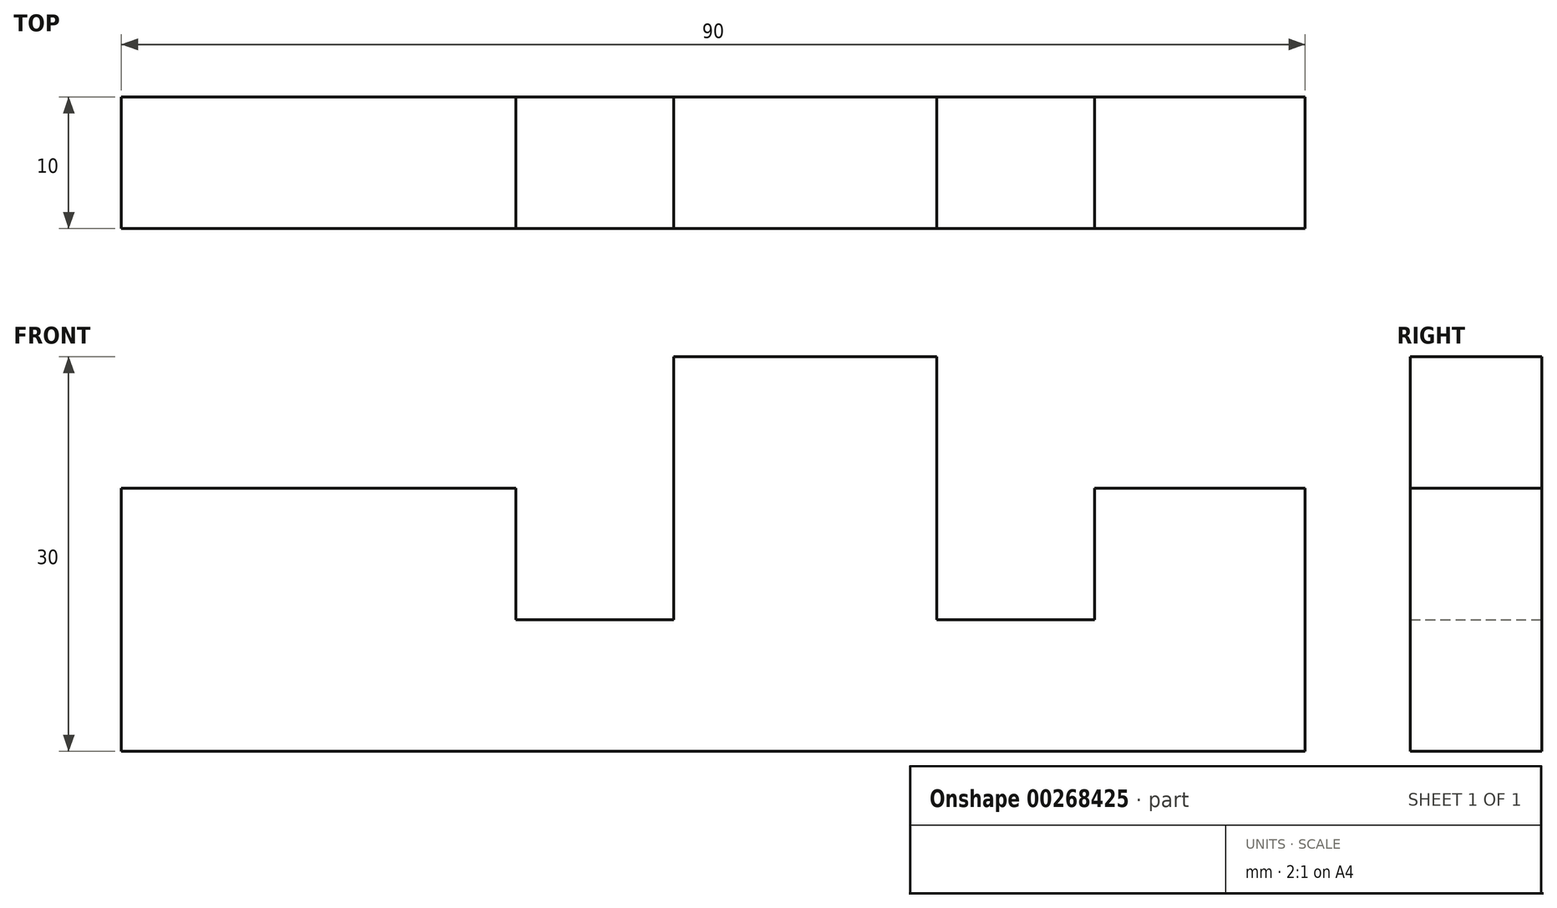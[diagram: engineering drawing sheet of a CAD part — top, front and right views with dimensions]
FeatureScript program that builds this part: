
annotation { "Feature Type Name" : "Feature", "Feature Type Description" : "" }
export const myFeature = defineFeature(function(context is Context, id is Id, definition is map)
    precondition{}
    {
        {
            var Q0;
            Q0=qCreatedBy(makeId("Front.planeOp"),FACE);
            var sketch = newSketch(context, id + "F0", { "sketchPlane" : qUnion([Q0])});
            skLineSegment(sketch, "E0", {"start": v(0, 0) * mm, "end": v(90, 0) * mm});
            skLineSegment(sketch, "E1", {"start": v(0, 0) * mm, "end": v(0, 20) * mm});
            skLineSegment(sketch, "E2", {"start": v(0, 20) * mm, "end": v(30, 20) * mm});
            skLineSegment(sketch, "E3", {"start": v(30, 20) * mm, "end": v(30, 10) * mm});
            skLineSegment(sketch, "E4", {"start": v(30, 10) * mm, "end": v(42, 10) * mm});
            skLineSegment(sketch, "E5", {"start": v(42, 10) * mm, "end": v(42, 30) * mm});
            skLineSegment(sketch, "E6", {"start": v(42, 30) * mm, "end": v(62, 30) * mm});
            skLineSegment(sketch, "E7", {"start": v(62, 30) * mm, "end": v(62, 10) * mm});
            skLineSegment(sketch, "E8", {"start": v(62, 10) * mm, "end": v(74, 10) * mm});
            skLineSegment(sketch, "E9", {"start": v(74, 10) * mm, "end": v(74, 20) * mm});
            skLineSegment(sketch, "E10", {"start": v(74, 20) * mm, "end": v(90, 20) * mm});
            skLineSegment(sketch, "E11", {"start": v(90, 20) * mm, "end": v(90, 0) * mm});
            skSolve(sketch);
        }
        {
            var Q0;
            Q0 = qSketchRegion(id + "F0", true);
            extrude(context, id + "F1", {"entities" : qUnion([Q0]), "depth" : 10 * mm});
        }
    });
